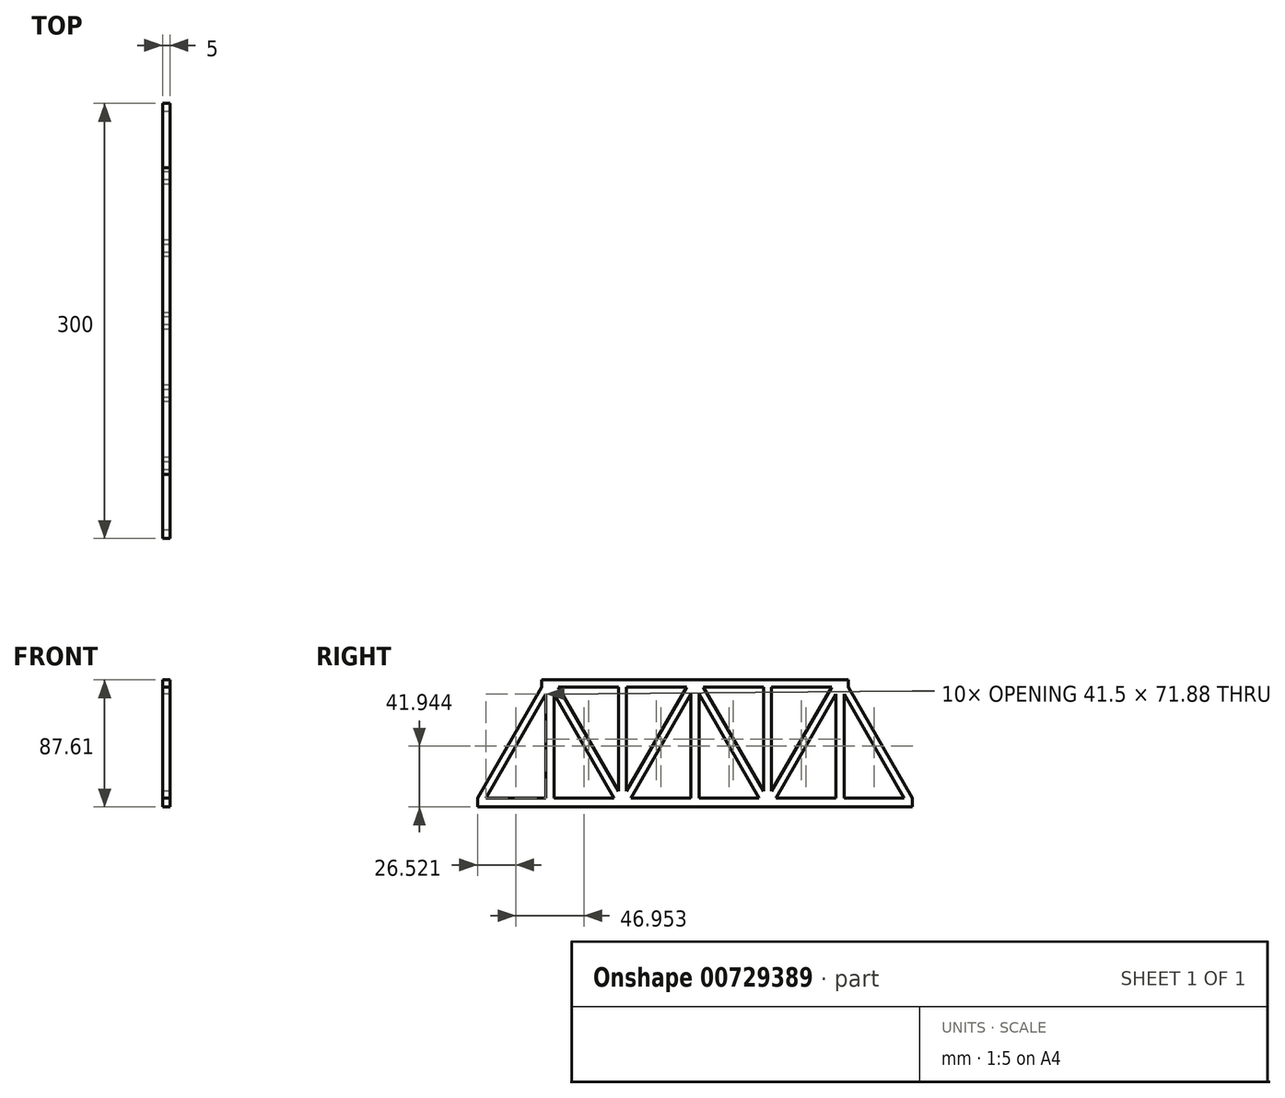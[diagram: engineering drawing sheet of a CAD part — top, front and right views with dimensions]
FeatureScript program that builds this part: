
annotation { "Feature Type Name" : "Feature", "Feature Type Description" : "" }
export const myFeature = defineFeature(function(context is Context, id is Id, definition is map)
    precondition{}
    {
        {
            var Q0;
            Q0=qCreatedBy(makeId("Right.planeOp"),FACE);
            var sketch = newSketch(context, id + "F0", { "sketchPlane" : qUnion([Q0])});
            skLineSegment(sketch, "E0.bottom", {"start": v(150.12, -38.73) * mm, "end": v(-149.88, -38.73) * mm});
            skLineSegment(sketch, "E0.top", {"start": v(150.12, -32.73) * mm, "end": v(-149.88, -32.73) * mm});
            skLineSegment(sketch, "E0.left", {"start": v(150.12, -38.73) * mm, "end": v(150.12, -32.73) * mm});
            skLineSegment(sketch, "E0.right", {"start": v(-149.88, -38.73) * mm, "end": v(-149.88, -32.73) * mm});
            skPoint(sketch, "E0.middle", {"position": v(0.12, -35.73) * mm});
            skLineSegment(sketch, "E1", {"start": v(5.9, 43.88) * mm, "end": v(50.12, -32.73) * mm});
            skLineSegment(sketch, "E2", {"start": v(-144.1, -32.73) * mm, "end": v(-99.88, 43.88) * mm});
            skLineSegment(sketch, "E3", {"start": v(-99.88, 43.88) * mm, "end": v(-55.66, -32.73) * mm});
            skLineSegment(sketch, "E4", {"start": v(-149.88, -32.73) * mm, "end": v(-105.66, 43.88) * mm});
            skLineSegment(sketch, "E5", {"start": v(-49.88, -32.73) * mm, "end": v(-94.1, 43.88) * mm});
            skLineSegment(sketch, "E6", {"start": v(-44.1, -32.73) * mm, "end": v(0.12, 43.88) * mm});
            skPoint(sketch, "E6.endSnap0", {"position": v(0.12, -32.73) * mm});
            skLineSegment(sketch, "E7", {"start": v(0.12, 43.88) * mm, "end": v(44.34, -32.73) * mm});
            skLineSegment(sketch, "E8", {"start": v(-49.88, -32.73) * mm, "end": v(-5.66, 43.88) * mm});
            skLineSegment(sketch, "E9", {"start": v(55.9, -32.73) * mm, "end": v(100.12, 43.88) * mm});
            skLineSegment(sketch, "E10", {"start": v(100.12, 43.88) * mm, "end": v(144.34, -32.73) * mm});
            skLineSegment(sketch, "E11", {"start": v(50.12, -32.73) * mm, "end": v(94.34, 43.88) * mm});
            skLineSegment(sketch, "E12", {"start": v(150.12, -32.73) * mm, "end": v(105.9, 43.88) * mm});
            skLineSegment(sketch, "E13", {"start": v(-105.66, 43.88) * mm, "end": v(105.9, 43.88) * mm});
            skLineSegment(sketch, "E14", {"start": v(-105.66, 43.88) * mm, "end": v(-105.66, 48.88) * mm});
            skLineSegment(sketch, "E15", {"start": v(-105.66, 48.88) * mm, "end": v(105.9, 48.88) * mm});
            skLineSegment(sketch, "E16", {"start": v(105.9, 48.88) * mm, "end": v(105.9, 43.88) * mm});
            skLineSegment(sketch, "E17", {"start": v(-102.6, 39.15) * mm, "end": v(-102.6, -32.73) * mm});
            skLineSegment(sketch, "E18", {"start": v(-102.6, -32.73) * mm, "end": v(-97.16, -32.73) * mm});
            skLineSegment(sketch, "E19", {"start": v(-97.16, -32.73) * mm, "end": v(-97.16, 39.15) * mm});
            skLineSegment(sketch, "E20", {"start": v(-52.6, -28) * mm, "end": v(-52.6, 43.88) * mm});
            skLineSegment(sketch, "E21", {"start": v(-52.6, 43.88) * mm, "end": v(-47.16, 43.88) * mm});
            skLineSegment(sketch, "E22", {"start": v(-47.16, 43.88) * mm, "end": v(-47.16, -28) * mm});
            skLineSegment(sketch, "E23", {"start": v(-2.6, 39.15) * mm, "end": v(-2.6, -32.73) * mm});
            skLineSegment(sketch, "E24", {"start": v(2.84, 39.15) * mm, "end": v(2.84, -32.73) * mm});
            skLineSegment(sketch, "E25", {"start": v(47.4, 43.88) * mm, "end": v(47.4, -28) * mm});
            skLineSegment(sketch, "E26", {"start": v(52.84, 43.88) * mm, "end": v(52.84, -28) * mm});
            skLineSegment(sketch, "E27", {"start": v(97.4, 39.15) * mm, "end": v(97.4, -32.73) * mm});
            skLineSegment(sketch, "E28", {"start": v(102.84, -32.73) * mm, "end": v(102.84, 39.15) * mm});
            skSolve(sketch);
        }
        {
            var Q0;
            {var subQ0=sQuery(id+"F0.wireOp",EDGE,"E4");Q0=makeQuery(id+"F0.imprint","IMPRINT",FACE,{"disambiguationData":[TD([[makeQuery(id+"F0.imprint","IMPRINT",EDGE,{"derivedFrom":subQ0}),-1.0]])]});}
            var Q1;
            {var subQ4=sQuery(id+"F0.wireOp",EDGE,"E17");Q1=makeQuery(id+"F0.imprint","IMPRINT",FACE,{"disambiguationData":[TD([[makeQuery(id+"F0.imprint","IMPRINT",EDGE,{"derivedFrom":subQ4}),1.0]])]});}
            var Q2;
            Q2=makeQuery(id+"F0.imprint","IMPRINT",FACE,{"disambiguationData":[TD([[makeQuery(id+"F0.imprint","IMPRINT",EDGE,{"derivedFrom":sQuery(id+"F0.wireOp",EDGE,"E0.bottom")}),-1.0]])]});
            var Q3;
            {var subQ1=sQuery(id+"F0.wireOp",EDGE,"E0.top");var subQ4=sQuery(id+"F0.wireOp",EDGE,"E3");var subQ5=makeQuery(id+"F0.imprint","INTERSECT",VERTEX,{"derivedFrom":[subQ1,subQ4]});Q3=makeQuery(id+"F0.imprint","IMPRINT",FACE,{"disambiguationData":[TD([[makeQuery(id+"F0.imprint","IMPRINT",EDGE,{"disambiguationData":[TD([[subQ5,1.0]])],"derivedFrom":subQ4}),1.0]])]});}
            var Q4;
            {var subQ3=sQuery(id+"F0.wireOp",EDGE,"E20");Q4=makeQuery(id+"F0.imprint","IMPRINT",FACE,{"disambiguationData":[TD([[makeQuery(id+"F0.imprint","IMPRINT",EDGE,{"derivedFrom":subQ3}),-1.0]])]});}
            var Q5;
            {var subQ1=sQuery(id+"F0.wireOp",EDGE,"E6");var subQ4=sQuery(id+"F0.wireOp",EDGE,"E0.top");var subQ5=makeQuery(id+"F0.imprint","INTERSECT",VERTEX,{"derivedFrom":[subQ4,subQ1]});Q5=makeQuery(id+"F0.imprint","IMPRINT",FACE,{"disambiguationData":[TD([[makeQuery(id+"F0.imprint","IMPRINT",EDGE,{"disambiguationData":[TD([[subQ5,-1.0]])],"derivedFrom":subQ1}),1.0]])]});}
            var Q6;
            {var subQ0=sQuery(id+"F0.wireOp",EDGE,"E23");Q6=makeQuery(id+"F0.imprint","IMPRINT",FACE,{"disambiguationData":[TD([[makeQuery(id+"F0.imprint","IMPRINT",EDGE,{"derivedFrom":subQ0}),1.0]])]});}
            var Q7;
            {var subQ0=sQuery(id+"F0.wireOp",EDGE,"E13");var subQ4=sQuery(id+"F0.wireOp",EDGE,"E1");var subQ5=makeQuery(id+"F0.imprint","INTERSECT",VERTEX,{"derivedFrom":[subQ4,subQ0]});Q7=makeQuery(id+"F0.imprint","IMPRINT",FACE,{"disambiguationData":[TD([[makeQuery(id+"F0.imprint","IMPRINT",EDGE,{"disambiguationData":[TD([[subQ5,-1.0]])],"derivedFrom":subQ4}),-1.0]])]});}
            var Q8;
            {var subQ0=sQuery(id+"F0.wireOp",EDGE,"E25");Q8=makeQuery(id+"F0.imprint","IMPRINT",FACE,{"disambiguationData":[TD([[makeQuery(id+"F0.imprint","IMPRINT",EDGE,{"derivedFrom":subQ0}),1.0]])]});}
            var Q9;
            {var subQ1=sQuery(id+"F0.wireOp",EDGE,"E0.top");var subQ5=sQuery(id+"F0.wireOp",EDGE,"E9");var subQ8=makeQuery(id+"F0.imprint","INTERSECT",VERTEX,{"derivedFrom":[subQ1,subQ5]});Q9=makeQuery(id+"F0.imprint","IMPRINT",FACE,{"disambiguationData":[TD([[makeQuery(id+"F0.imprint","IMPRINT",EDGE,{"disambiguationData":[TD([[subQ8,-1.0]])],"derivedFrom":subQ5}),1.0]])]});}
            var Q10;
            {var subQ4=sQuery(id+"F0.wireOp",EDGE,"E27");Q10=makeQuery(id+"F0.imprint","IMPRINT",FACE,{"disambiguationData":[TD([[makeQuery(id+"F0.imprint","IMPRINT",EDGE,{"derivedFrom":subQ4}),1.0]])]});}
            var Q11;
            {var subQ0=sQuery(id+"F0.wireOp",EDGE,"E12");Q11=makeQuery(id+"F0.imprint","IMPRINT",FACE,{"disambiguationData":[TD([[makeQuery(id+"F0.imprint","IMPRINT",EDGE,{"derivedFrom":subQ0}),1.0]])]});}
            var Q12;
            {var subQ9=sQuery(id+"F0.wireOp",EDGE,"E14");Q12=makeQuery(id+"F0.imprint","IMPRINT",FACE,{"disambiguationData":[TD([[makeQuery(id+"F0.imprint","IMPRINT",EDGE,{"derivedFrom":subQ9}),-1.0]])]});}
            extrude(context, id + "F1", {"entities" : qUnion([Q0, Q1, Q2, Q3, Q4, Q5, Q6, Q7, Q8, Q9, Q10, Q11, Q12]), "depth" : 5 * mm, "offsetDistance" : 25 * mm});
        }
    });
